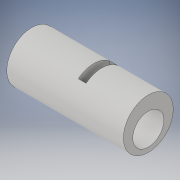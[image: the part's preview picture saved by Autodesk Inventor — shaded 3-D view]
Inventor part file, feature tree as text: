
AUTODESK INVENTOR PART (.ipt)
format: ipt  version: 2019 (Build 230136000, 136)  size: 256,000 bytes
history: native  units: in
note: dims shown in document units (in); Inventor stores cm internally (conversion verified against a paired STEP export)
features: sketch x9, extrude x4, revolve x1, loft x1, fillet x1, plane x1, other x1
ambient origin geometry x8: Origin, YZ Plane, XZ Plane, XY Plane, X Axis, Y Axis, Z Axis, Center Point
bodies: Solid1 (feature_tree)
feature tree (18):
  revolve  "Revolution1"  [1 undecoded]
  sketch  "Sketch2"  dims[d3=0.7874in d4=90.0deg]
  extrude  "Extrusion1"  TaperAngle=90.0deg  [1 undecoded]
  sketch  "Sketch4"  dims[d9=0.7874in d10=0.0in d11=90.0deg]
  sketch  "Sketch5"  dims[d12=0.0in d13=90.0deg d14=0.2362in]
  loft  "Loft1"
  fillet  "Fillet1"  Radius=0.3937in
  sketch  "Sketch6"  dims[d15=0.5118in d16=0.1969in d17=0.0in]
  plane  "Work Plane1"
  extrude  "Extrusion2"  TaperAngle=0.0deg  [1 undecoded]
  extrude  "Extrusion3"  Depth=0.2362in
  extrude  "Extrusion4"  Depth=0.1969in TaperAngle=0.0deg
  sketch  "Sketch1"  dims[d0=0.1181in d1=0.7874in]
  sketch  "Sketch3"  dims[d5=0.0591in d6=0.5118in d7=0.3937in d8=0.0in]
  other  "Edges1"
  sketch  "Sketch7"  dims[d18=0.6299in]
  sketch  "Sketch8"  dims[d19=0.7177in]
  sketch  "Sketch9"  dims[d22=0.3937in d24=0.1969in d25=0.0in d26=1.2598in d28=0.3937in d29=0.1199in d30=1.1811in d31=0.0in]
note: 3 required parameter values undecoded (feature->parameter linkage not recoverable at this tier; creation-order binding heuristic only, values carry confidence <= 0.55)